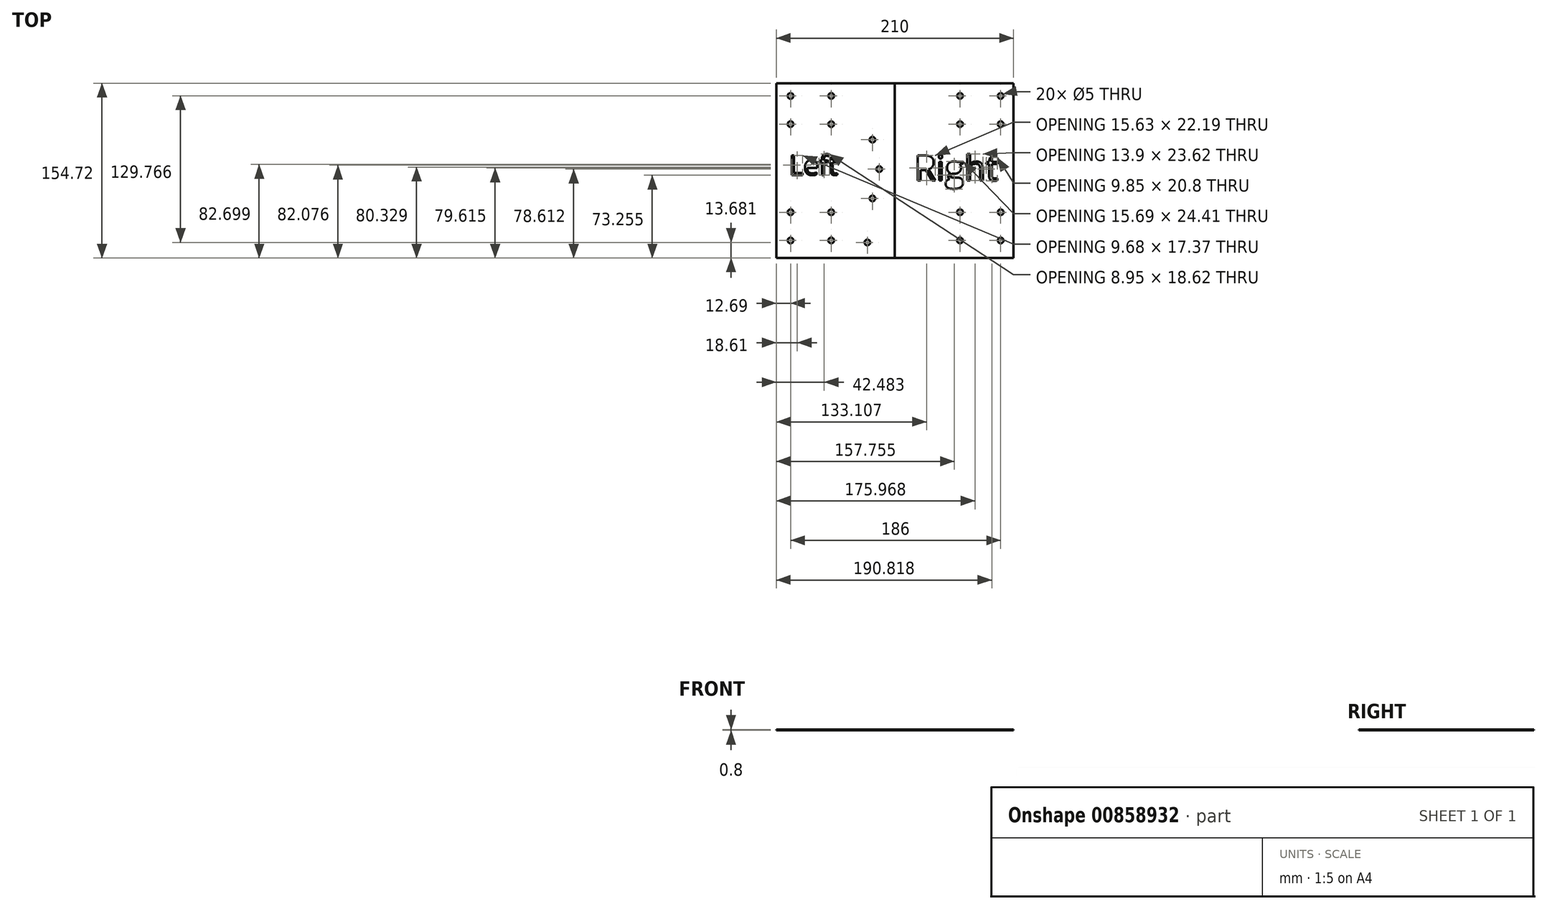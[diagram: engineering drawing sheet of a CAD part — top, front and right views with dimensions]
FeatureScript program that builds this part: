
annotation { "Feature Type Name" : "Feature", "Feature Type Description" : "" }
export const myFeature = defineFeature(function(context is Context, id is Id, definition is map)
    precondition{}
    {
        {
            var Q0;
            Q0=qCreatedBy(makeId("Top.planeOp"),FACE);
            var sketch = newSketch(context, id + "F0", { "sketchPlane" : qUnion([Q0])});
            skLineSegment(sketch, "E0.bottom", {"start": v(-75.52, -74.37) * mm, "end": v(194.48, -75.42) * mm});
            skLineSegment(sketch, "E0.left", {"start": v(-75.52, -74.37) * mm, "end": v(-75.52, 165.63) * mm});
            skCircle(sketch, "E1", {"center": v(-3.52, 26.36) * mm, "radius": 2.5 * mm});
            skCircle(sketch, "E2", {"center": v(-3.52, 51.36) * mm, "radius": 2.5 * mm});
            skCircle(sketch, "E3", {"center": v(-3.52, 129.36) * mm, "radius": 2.5 * mm});
            skCircle(sketch, "E4", {"center": v(-3.52, 154.36) * mm, "radius": 2.5 * mm});
            skCircle(sketch, "E5", {"center": v(32.48, 154.36) * mm, "radius": 2.5 * mm});
            skCircle(sketch, "E6", {"center": v(32.48, 129.36) * mm, "radius": 2.5 * mm});
            skCircle(sketch, "E7", {"center": v(32.48, 51.36) * mm, "radius": 2.5 * mm});
            skCircle(sketch, "E8", {"center": v(32.48, 26.36) * mm, "radius": 2.5 * mm});
            skCircle(sketch, "E9", {"center": v(146.48, 154.36) * mm, "radius": 2.5 * mm});
            skCircle(sketch, "E10", {"center": v(146.48, 129.36) * mm, "radius": 2.5 * mm});
            skCircle(sketch, "E11", {"center": v(146.48, 51.36) * mm, "radius": 2.5 * mm});
            skCircle(sketch, "E12", {"center": v(146.48, 26.36) * mm, "radius": 2.5 * mm});
            skCircle(sketch, "E13", {"center": v(182.48, 154.36) * mm, "radius": 2.5 * mm});
            skCircle(sketch, "E14", {"center": v(182.48, 129.36) * mm, "radius": 2.5 * mm});
            skCircle(sketch, "E15", {"center": v(182.48, 51.36) * mm, "radius": 2.5 * mm});
            skCircle(sketch, "E16", {"center": v(182.48, 26.36) * mm, "radius": 2.5 * mm});
            skCircle(sketch, "E17", {"center": v(64.48, 24.6) * mm, "radius": 2.5 * mm});
            skCircle(sketch, "E18", {"center": v(68.98, 63.57) * mm, "radius": 2.5 * mm});
            skCircle(sketch, "E19", {"center": v(74.98, 89.55) * mm, "radius": 2.5 * mm});
            skCircle(sketch, "E20", {"center": v(68.98, 115.57) * mm, "radius": 2.5 * mm});
            skLineSegment(sketch, "E21", {"start": v(-75.52, 165.63) * mm, "end": v(193.8, 165.63) * mm});
            skLineSegment(sketch, "E22", {"start": v(193.8, 165.63) * mm, "end": v(193.8, -75.42) * mm});
            skLineSegment(sketch, "E23.bottom", {"start": v(-75.52, -74.37) * mm, "end": v(193.8, -74.37) * mm});
            skLineSegment(sketch, "E23.top", {"start": v(-75.52, 10.91) * mm, "end": v(193.8, 10.91) * mm});
            skLineSegment(sketch, "E23.left", {"start": v(-75.52, -74.37) * mm, "end": v(-75.52, 10.91) * mm});
            skLineSegment(sketch, "E23.right", {"start": v(193.8, -74.37) * mm, "end": v(193.8, 10.91) * mm});
            skLineSegment(sketch, "E24.bottom", {"start": v(-75.52, 165.63) * mm, "end": v(-16.2, 165.63) * mm});
            skLineSegment(sketch, "E24.top", {"start": v(-75.52, 10.91) * mm, "end": v(-16.2, 10.91) * mm});
            skLineSegment(sketch, "E24.left", {"start": v(-75.52, 165.63) * mm, "end": v(-75.52, 10.91) * mm});
            skLineSegment(sketch, "E24.right", {"start": v(-16.2, 165.63) * mm, "end": v(-16.2, 10.91) * mm});
            skLineSegment(sketch, "E25", {"start": v(88.8, 165.63) * mm, "end": v(88.8, 10.91) * mm});
            skText(sketch, "E26", { "text": "Left", "fontName": "OpenSans-Regular.ttf"});
            skText(sketch, "E27", { "text": "Right", "fontName": "OpenSans-Regular.ttf"});
            const initialGuessF0  = {"E26": [-0.00483, 0.0843, 1, 0, 0.01752], "E27": [0.10603, 0.07943, 1, 0, 0.02238]};
            skSetInitialGuess(sketch, initialGuessF0);
            skSolve(sketch);
        }
        {
            var Q0;
            Q0=makeQuery(id+"F0.imprint","IMPRINT",FACE,{"disambiguationData":[TD([[makeQuery(id+"F0.imprint","IMPRINT",EDGE,{"derivedFrom":sQuery(id+"F0.wireOp",EDGE,"E1")}),-1.0]])]});
            extrude(context, id + "F1", {"entities" : qUnion([Q0]), "depth" : 0.8 * mm, "offsetDistance" : 25 * mm});
        }
        {
            var Q0;
            Q0=makeQuery(id+"F0.imprint","IMPRINT",FACE,{"disambiguationData":[TD([[makeQuery(id+"F0.imprint","IMPRINT",EDGE,{"derivedFrom":sQuery(id+"F0.wireOp",EDGE,"E9")}),-1.0]])]});
            extrude(context, id + "F2", {"entities" : qUnion([Q0]), "depth" : 0.8 * mm, "offsetDistance" : 25 * mm});
        }
    });
